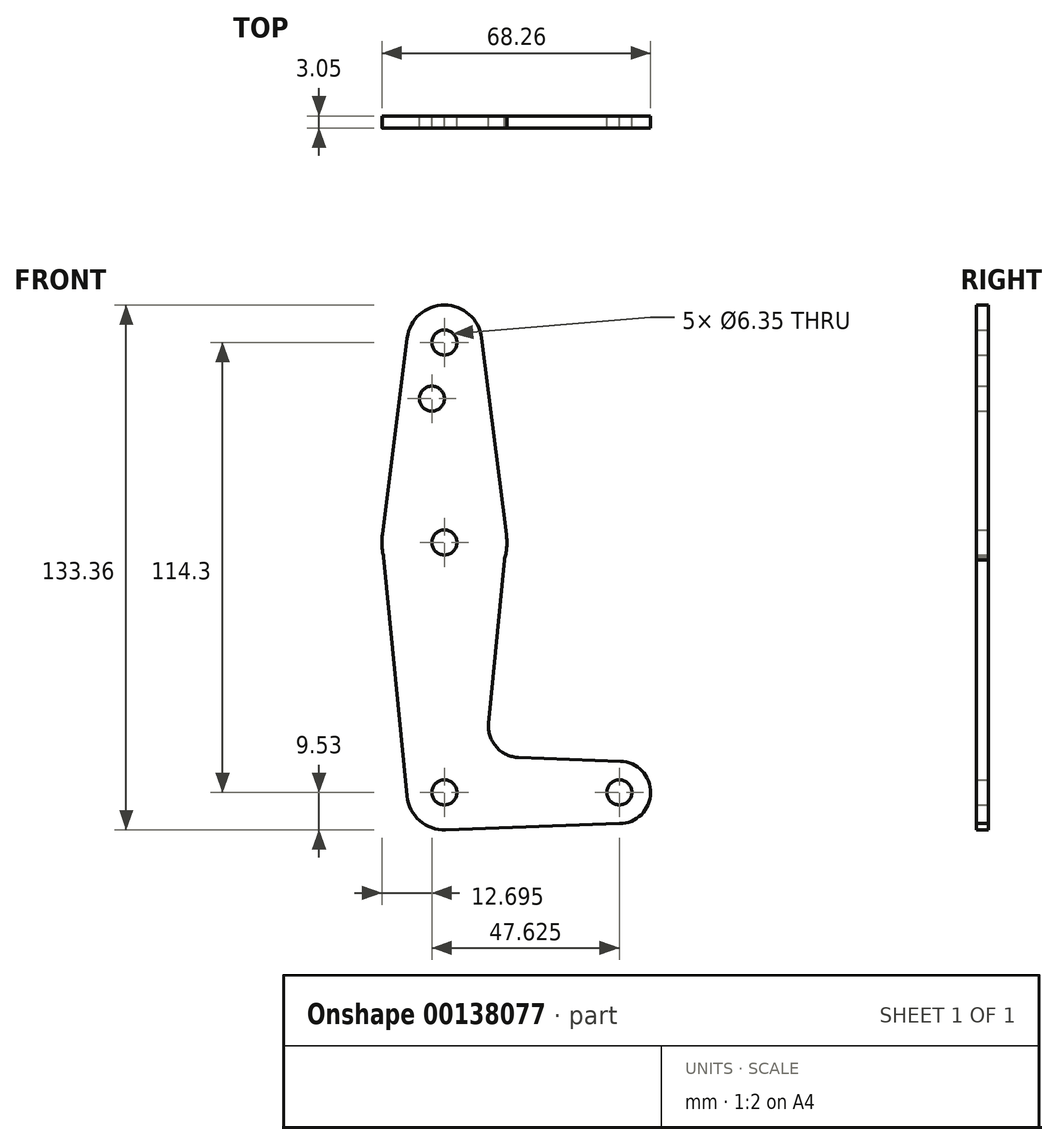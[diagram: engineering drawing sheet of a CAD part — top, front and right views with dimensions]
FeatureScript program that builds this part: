
annotation { "Feature Type Name" : "Feature", "Feature Type Description" : "" }
export const myFeature = defineFeature(function(context is Context, id is Id, definition is map)
    precondition{}
    {
        {
            var Q0;
            Q0=qCreatedBy(makeId("Front.planeOp"),FACE);
            var sketch = newSketch(context, id + "F0", { "sketchPlane" : qUnion([Q0])});
            skLineSegment(sketch, "E0", {"start": v(0, 0) * mm, "end": v(0, 114.3) * mm, "construction": true});
            skLineSegment(sketch, "E1", {"start": v(0, 0) * mm, "end": v(44.45, 0) * mm, "construction": true});
            skCircle(sketch, "E2", {"center": v(0, 114.3) * mm, "radius": 9.53 * mm});
            skCircle(sketch, "E3", {"center": v(0, 63.5) * mm, "radius": 15.88 * mm});
            skCircle(sketch, "E4", {"center": v(0, 0) * mm, "radius": 9.53 * mm});
            skCircle(sketch, "E5", {"center": v(44.45, 0) * mm, "radius": 7.94 * mm});
            skLineSegment(sketch, "E6", {"start": v(9.45, 115.5) * mm, "end": v(15.75, 65.48) * mm});
            skLineSegment(sketch, "E7", {"start": v(-9.45, 115.5) * mm, "end": v(-15.75, 65.48) * mm});
            skLineSegment(sketch, "E8", {"start": v(15.22, 59) * mm, "end": v(11.25, 17.56) * mm});
            skLineSegment(sketch, "E9", {"start": v(-15.44, 59.8) * mm, "end": v(-9.48, -0.93) * mm});
            skLineSegment(sketch, "E10", {"start": v(18.88, 8.85) * mm, "end": v(44.73, 7.93) * mm});
            skLineSegment(sketch, "E11", {"start": v(44.45, -7.94) * mm, "end": v(0, -9.53) * mm});
            skCircle(sketch, "E12", {"center": v(0, 114.3) * mm, "radius": 3.18 * mm});
            skCircle(sketch, "E13", {"center": v(-3.17, 100.03) * mm, "radius": 3.18 * mm});
            skCircle(sketch, "E14", {"center": v(0, 63.5) * mm, "radius": 3.18 * mm});
            skCircle(sketch, "E15", {"center": v(0, 0) * mm, "radius": 3.18 * mm});
            skCircle(sketch, "E16", {"center": v(44.45, 0) * mm, "radius": 3.18 * mm});
            skArc(sketch, "E17.filletArc", {"start": v(11.25, 17.56) * mm, "mid": v(13.19, 11.56) * mm, "end": v(18.88, 8.85) * mm});
            skSolve(sketch);
        }
        {
            var Q0;
            Q0 = qSketchRegion(id + "F0", true);
            extrude(context, id + "F1", {"entities" : qUnion([Q0]), "depth" : 3.05 * mm});
        }
    });
